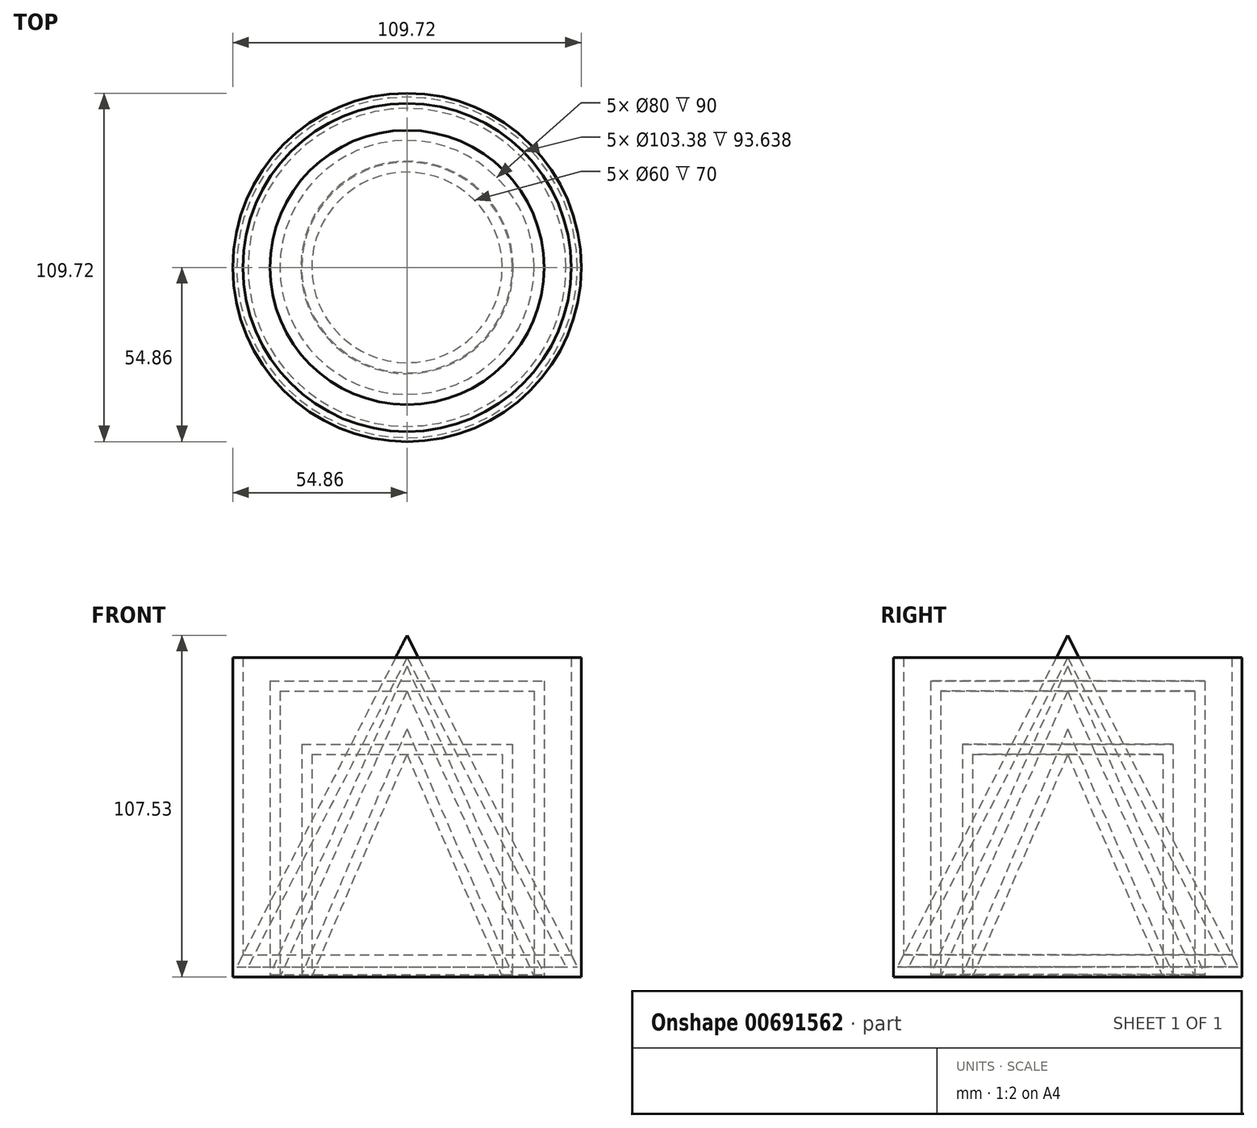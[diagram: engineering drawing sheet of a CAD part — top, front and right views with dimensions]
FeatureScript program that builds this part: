
annotation { "Feature Type Name" : "Feature", "Feature Type Description" : "" }
export const myFeature = defineFeature(function(context is Context, id is Id, definition is map)
    precondition{}
    {
        {
            var Q0;
            Q0=qCreatedBy(makeId("Front.planeOp"),FACE);
            var sketch = newSketch(context, id + "F0", { "sketchPlane" : qUnion([Q0])});
            skLineSegment(sketch, "E0", {"start": v(0, 0) * mm, "end": v(-54.86, 0) * mm});
            skLineSegment(sketch, "E1", {"start": v(-54.86, 0) * mm, "end": v(-54.86, 100.58) * mm});
            skLineSegment(sketch, "E2", {"start": v(-54.86, 100.58) * mm, "end": v(-51.69, 100.58) * mm});
            skLineSegment(sketch, "E3.0", {"start": v(-51.69, 3.17) * mm, "end": v(-51.69, 129.8) * mm});
            skLineSegment(sketch, "E4.0", {"start": v(0, 3.18) * mm, "end": v(-53.63, 3.17) * mm});
            skLineSegment(sketch, "E5", {"start": v(0, 0) * mm, "end": v(0, 3.18) * mm});
            skLineSegment(sketch, "E6", {"start": v(0, 3.18) * mm, "end": v(0, 52.66) * mm});
            skLineSegment(sketch, "E7", {"start": v(-50.06, 3.17) * mm, "end": v(0, 100.58) * mm});
            skLineSegment(sketch, "E8", {"start": v(0, 100.58) * mm, "end": v(0, 107.53) * mm});
            skLineSegment(sketch, "E9", {"start": v(-54.86, 0) * mm, "end": v(-51.69, 0) * mm});
            skLineSegment(sketch, "E10.trimOffspring", {"start": v(-53.63, 3.17) * mm, "end": v(0, 107.53) * mm});
            skSolve(sketch);
        }
        {
            var Q0;
            {var subQ0=sQuery(id+"F0.wireOp",EDGE,"E0");Q0=makeQuery(id+"F0.imprint","IMPRINT",FACE,{"disambiguationData":[TD([[makeQuery(id+"F0.imprint","IMPRINT",EDGE,{"derivedFrom":subQ0}),-1.0]])]});}
            var Q1;
            {var subQ0=sQuery(id+"F0.wireOp",EDGE,"E2");Q1=makeQuery(id+"F0.imprint","IMPRINT",FACE,{"disambiguationData":[TD([[makeQuery(id+"F0.imprint","IMPRINT",EDGE,{"derivedFrom":subQ0}),-1.0]])]});}
            var Q2;
            {var subQ5=sQuery(id+"F0.wireOp",EDGE,"E9");var subQ9=sQuery(id+"F0.wireOp",EDGE,"E1");var subQ10=makeQuery(id+"F0.imprint","INTERSECT",VERTEX,{"derivedFrom":[subQ9,subQ5]});Q2=makeQuery(id+"F0.imprint","IMPRINT",FACE,{"disambiguationData":[TD([[makeQuery(id+"F0.imprint","IMPRINT",EDGE,{"disambiguationData":[TD([[subQ10,-1.0]])],"derivedFrom":subQ9}),-1.0]])]});}
            var Q3;
            Q3=sQuery(id+"F0.wireOp",EDGE,"E6");
            revolve(context, id + "F1", {"entities" : qUnion([Q0, Q1, Q2]), "axis" : qUnion([Q3]), "revolveType" : RevolveType.FULL});
        }
        {
            var Q0;
            {var subQ0=sQuery(id+"F0.wireOp",EDGE,"E8");Q0=makeQuery(id+"F0.imprint","IMPRINT",FACE,{"disambiguationData":[TD([[makeQuery(id+"F0.imprint","IMPRINT",EDGE,{"derivedFrom":subQ0}),1.0]])]});}
            var Q1;
            {var subQ0=sQuery(id+"F0.wireOp",EDGE,"E4.0");var subQ1=sQuery(id+"F0.wireOp",EDGE,"E3.0");var subQ2=makeQuery(id+"F0.imprint","INTERSECT",VERTEX,{"derivedFrom":[subQ1,subQ0]});Q1=makeQuery(id+"F0.imprint","IMPRINT",FACE,{"disambiguationData":[TD([[makeQuery(id+"F0.imprint","IMPRINT",EDGE,{"disambiguationData":[TD([[subQ2,-1.0]])],"derivedFrom":subQ1}),1.0]])]});}
            var Q2;
            Q2=sQuery(id+"F0.wireOp",EDGE,"E6");
            revolve(context, id + "F2", {"entities" : qUnion([Q0, Q1]), "axis" : qUnion([Q2]), "revolveType" : RevolveType.FULL, "surfaceOperationType" : NewSurfaceOperationType.NEW});
        }
        {
            var Q0;
            Q0=qCreatedBy(makeId("Front.planeOp"),FACE);
            var sketch = newSketch(context, id + "F3", { "sketchPlane" : qUnion([Q0])});
            skLineSegment(sketch, "E11", {"start": v(0, 0) * mm, "end": v(-40, 0) * mm});
            skLineSegment(sketch, "E12", {"start": v(0, 0) * mm, "end": v(0, 90) * mm});
            skLineSegment(sketch, "E13", {"start": v(-40, 0) * mm, "end": v(0, 90) * mm});
            skLineSegment(sketch, "E14.0", {"start": v(-43.47, 0) * mm, "end": v(0, 97.82) * mm});
            skLineSegment(sketch, "E15", {"start": v(-40, 0) * mm, "end": v(-43.47, 0) * mm});
            skLineSegment(sketch, "E16", {"start": v(-40, 0) * mm, "end": v(-40, 90) * mm});
            skLineSegment(sketch, "E17", {"start": v(-40, 90) * mm, "end": v(0, 90) * mm});
            skLineSegment(sketch, "E18", {"start": v(0, 90) * mm, "end": v(0, 97.82) * mm});
            skLineSegment(sketch, "E19.0", {"start": v(-43.18, 0) * mm, "end": v(-43.18, 93.17) * mm});
            skLineSegment(sketch, "E20.0", {"start": v(-43.18, 93.17) * mm, "end": v(0, 93.17) * mm});
            skSolve(sketch);
        }
        {
            var Q0;
            {var subQ3=sQuery(id+"F3.wireOp",EDGE,"E14.0");var subQ8=sQuery(id+"F3.wireOp",EDGE,"E19.0");var subQ10=makeQuery(id+"F3.imprint","INTERSECT",VERTEX,{"derivedFrom":[subQ3,subQ8]});Q0=makeQuery(id+"F3.imprint","IMPRINT",FACE,{"disambiguationData":[TD([[makeQuery(id+"F3.imprint","IMPRINT",EDGE,{"disambiguationData":[TD([[subQ10,-1.0]])],"derivedFrom":subQ3}),1.0]])]});}
            var Q1;
            {var subQ0=sQuery(id+"F3.wireOp",EDGE,"E20.0");var subQ1=sQuery(id+"F3.wireOp",EDGE,"E14.0");var subQ2=makeQuery(id+"F3.imprint","INTERSECT",VERTEX,{"derivedFrom":[subQ1,subQ0]});Q1=makeQuery(id+"F3.imprint","IMPRINT",FACE,{"disambiguationData":[TD([[makeQuery(id+"F3.imprint","IMPRINT",EDGE,{"disambiguationData":[TD([[subQ2,1.0]])],"derivedFrom":subQ1}),-1.0]])]});}
            var Q2;
            {var subQ0=sQuery(id+"F3.wireOp",EDGE,"E19.0");var subQ1=sQuery(id+"F3.wireOp",EDGE,"E14.0");var subQ2=makeQuery(id+"F3.imprint","INTERSECT",VERTEX,{"derivedFrom":[subQ1,subQ0]});Q2=makeQuery(id+"F3.imprint","IMPRINT",FACE,{"disambiguationData":[TD([[makeQuery(id+"F3.imprint","IMPRINT",EDGE,{"disambiguationData":[TD([[subQ2,-1.0]])],"derivedFrom":subQ1}),-1.0]])]});}
            var Q3;
            Q3=sQuery(id+"F3.wireOp",EDGE,"E12");
            revolve(context, id + "F4", {"surfaceOperationType" : NewSurfaceOperationType.NEW, "entities" : qUnion([Q0, Q1, Q2]), "axis" : qUnion([Q3]), "revolveType" : RevolveType.FULL});
        }
        {
            var Q0;
            {var subQ0=sQuery(id+"F3.wireOp",EDGE,"E13");Q0=makeQuery(id+"F3.imprint","IMPRINT",FACE,{"disambiguationData":[TD([[makeQuery(id+"F3.imprint","IMPRINT",EDGE,{"derivedFrom":subQ0}),1.0]])]});}
            var Q1;
            {var subQ4=sQuery(id+"F3.wireOp",EDGE,"E18");Q1=makeQuery(id+"F3.imprint","IMPRINT",FACE,{"disambiguationData":[TD([[makeQuery(id+"F3.imprint","IMPRINT",EDGE,{"derivedFrom":subQ4}),1.0]])]});}
            var Q2;
            {var subQ0=sQuery(id+"F3.wireOp",EDGE,"E19.0");var subQ1=sQuery(id+"F3.wireOp",EDGE,"E14.0");var subQ2=makeQuery(id+"F3.imprint","INTERSECT",VERTEX,{"derivedFrom":[subQ1,subQ0]});Q2=makeQuery(id+"F3.imprint","IMPRINT",FACE,{"disambiguationData":[TD([[makeQuery(id+"F3.imprint","IMPRINT",EDGE,{"disambiguationData":[TD([[subQ2,-1.0]])],"derivedFrom":subQ1}),-1.0]])]});}
            var Q3;
            {var subQ0=sQuery(id+"F3.wireOp",EDGE,"E20.0");var subQ1=sQuery(id+"F3.wireOp",EDGE,"E14.0");var subQ2=makeQuery(id+"F3.imprint","INTERSECT",VERTEX,{"derivedFrom":[subQ1,subQ0]});Q3=makeQuery(id+"F3.imprint","IMPRINT",FACE,{"disambiguationData":[TD([[makeQuery(id+"F3.imprint","IMPRINT",EDGE,{"disambiguationData":[TD([[subQ2,1.0]])],"derivedFrom":subQ1}),-1.0]])]});}
            var Q4;
            Q4=sQuery(id+"F3.wireOp",EDGE,"E12");
            revolve(context, id + "F5", {"surfaceOperationType" : NewSurfaceOperationType.NEW, "entities" : qUnion([Q0, Q1, Q2, Q3]), "axis" : qUnion([Q4]), "revolveType" : RevolveType.FULL});
        }
        {
            var Q0;
            Q0=qCreatedBy(makeId("Front.planeOp"),FACE);
            var sketch = newSketch(context, id + "F6", { "sketchPlane" : qUnion([Q0])});
            skLineSegment(sketch, "E21", {"start": v(0, 0) * mm, "end": v(30, 0) * mm});
            skLineSegment(sketch, "E22", {"start": v(0, 0) * mm, "end": v(0, 70) * mm});
            skLineSegment(sketch, "E23", {"start": v(0, 70) * mm, "end": v(30, 0) * mm});
            skLineSegment(sketch, "E24", {"start": v(30, 0) * mm, "end": v(30, 70) * mm});
            skLineSegment(sketch, "E25", {"start": v(0, 70) * mm, "end": v(30, 70) * mm});
            skLineSegment(sketch, "E26.0", {"start": v(0, 78.06) * mm, "end": v(33.45, 0) * mm});
            skLineSegment(sketch, "E27.0", {"start": v(33.17, 0) * mm, "end": v(33.17, 73.17) * mm});
            skLineSegment(sketch, "E28.0", {"start": v(0, 73.17) * mm, "end": v(33.17, 73.17) * mm});
            skLineSegment(sketch, "E29", {"start": v(30, 0) * mm, "end": v(33.45, 0) * mm});
            skLineSegment(sketch, "E30", {"start": v(0, 70) * mm, "end": v(0, 78.06) * mm});
            skSolve(sketch);
        }
        {
            var Q0;
            {var subQ0=sQuery(id+"F6.wireOp",EDGE,"E23");Q0=makeQuery(id+"F6.imprint","IMPRINT",FACE,{"disambiguationData":[TD([[makeQuery(id+"F6.imprint","IMPRINT",EDGE,{"derivedFrom":subQ0}),1.0]])]});}
            var Q1;
            {var subQ0=sQuery(id+"F6.wireOp",EDGE,"E30");Q1=makeQuery(id+"F6.imprint","IMPRINT",FACE,{"disambiguationData":[TD([[makeQuery(id+"F6.imprint","IMPRINT",EDGE,{"derivedFrom":subQ0}),-1.0]])]});}
            var Q2;
            {var subQ3=sQuery(id+"F6.wireOp",EDGE,"E26.0");var subQ5=sQuery(id+"F6.wireOp",EDGE,"E27.0");var subQ6=makeQuery(id+"F6.imprint","INTERSECT",VERTEX,{"derivedFrom":[subQ3,subQ5]});Q2=makeQuery(id+"F6.imprint","IMPRINT",FACE,{"disambiguationData":[TD([[makeQuery(id+"F6.imprint","IMPRINT",EDGE,{"disambiguationData":[TD([[subQ6,1.0]])],"derivedFrom":subQ3}),-1.0]])]});}
            var Q3;
            {var subQ0=sQuery(id+"F6.wireOp",EDGE,"E29");var subQ1=sQuery(id+"F6.wireOp",EDGE,"E26.0");var subQ2=makeQuery(id+"F6.imprint","INTERSECT",VERTEX,{"derivedFrom":[subQ1,subQ0]});Q3=makeQuery(id+"F6.imprint","IMPRINT",FACE,{"disambiguationData":[TD([[makeQuery(id+"F6.imprint","IMPRINT",EDGE,{"disambiguationData":[TD([[subQ2,1.0]])],"derivedFrom":subQ1}),-1.0]])]});}
            var Q4;
            {var subQ3=sQuery(id+"F6.wireOp",EDGE,"E26.0");var subQ5=sQuery(id+"F6.wireOp",EDGE,"E28.0");var subQ6=makeQuery(id+"F6.imprint","INTERSECT",VERTEX,{"derivedFrom":[subQ3,subQ5]});Q4=makeQuery(id+"F6.imprint","IMPRINT",FACE,{"disambiguationData":[TD([[makeQuery(id+"F6.imprint","IMPRINT",EDGE,{"disambiguationData":[TD([[subQ6,-1.0]])],"derivedFrom":subQ3}),-1.0]])]});}
            var Q5;
            Q5=sQuery(id+"F6.wireOp",EDGE,"E22");
            revolve(context, id + "F7", {"surfaceOperationType" : NewSurfaceOperationType.NEW, "entities" : qUnion([Q0, Q1, Q2, Q3, Q4]), "axis" : qUnion([Q5]), "revolveType" : RevolveType.FULL});
        }
        {
            var Q0;
            {var subQ3=sQuery(id+"F6.wireOp",EDGE,"E24");var subQ7=sQuery(id+"F6.wireOp",EDGE,"E25");var subQ9=makeQuery(id+"F6.imprint","INTERSECT",VERTEX,{"derivedFrom":[subQ3,subQ7]});Q0=makeQuery(id+"F6.imprint","IMPRINT",FACE,{"disambiguationData":[TD([[makeQuery(id+"F6.imprint","IMPRINT",EDGE,{"disambiguationData":[TD([[subQ9,1.0]])],"derivedFrom":subQ3}),-1.0]])]});}
            var Q1;
            {var subQ3=sQuery(id+"F6.wireOp",EDGE,"E26.0");var subQ5=sQuery(id+"F6.wireOp",EDGE,"E28.0");var subQ6=makeQuery(id+"F6.imprint","INTERSECT",VERTEX,{"derivedFrom":[subQ3,subQ5]});Q1=makeQuery(id+"F6.imprint","IMPRINT",FACE,{"disambiguationData":[TD([[makeQuery(id+"F6.imprint","IMPRINT",EDGE,{"disambiguationData":[TD([[subQ6,-1.0]])],"derivedFrom":subQ3}),-1.0]])]});}
            var Q2;
            {var subQ3=sQuery(id+"F6.wireOp",EDGE,"E26.0");var subQ5=sQuery(id+"F6.wireOp",EDGE,"E27.0");var subQ6=makeQuery(id+"F6.imprint","INTERSECT",VERTEX,{"derivedFrom":[subQ3,subQ5]});Q2=makeQuery(id+"F6.imprint","IMPRINT",FACE,{"disambiguationData":[TD([[makeQuery(id+"F6.imprint","IMPRINT",EDGE,{"disambiguationData":[TD([[subQ6,1.0]])],"derivedFrom":subQ3}),-1.0]])]});}
            var Q3;
            Q3=sQuery(id+"F6.wireOp",EDGE,"E22");
            revolve(context, id + "F8", {"surfaceOperationType" : NewSurfaceOperationType.NEW, "entities" : qUnion([Q0, Q1, Q2]), "axis" : qUnion([Q3]), "revolveType" : RevolveType.FULL});
        }
    });
